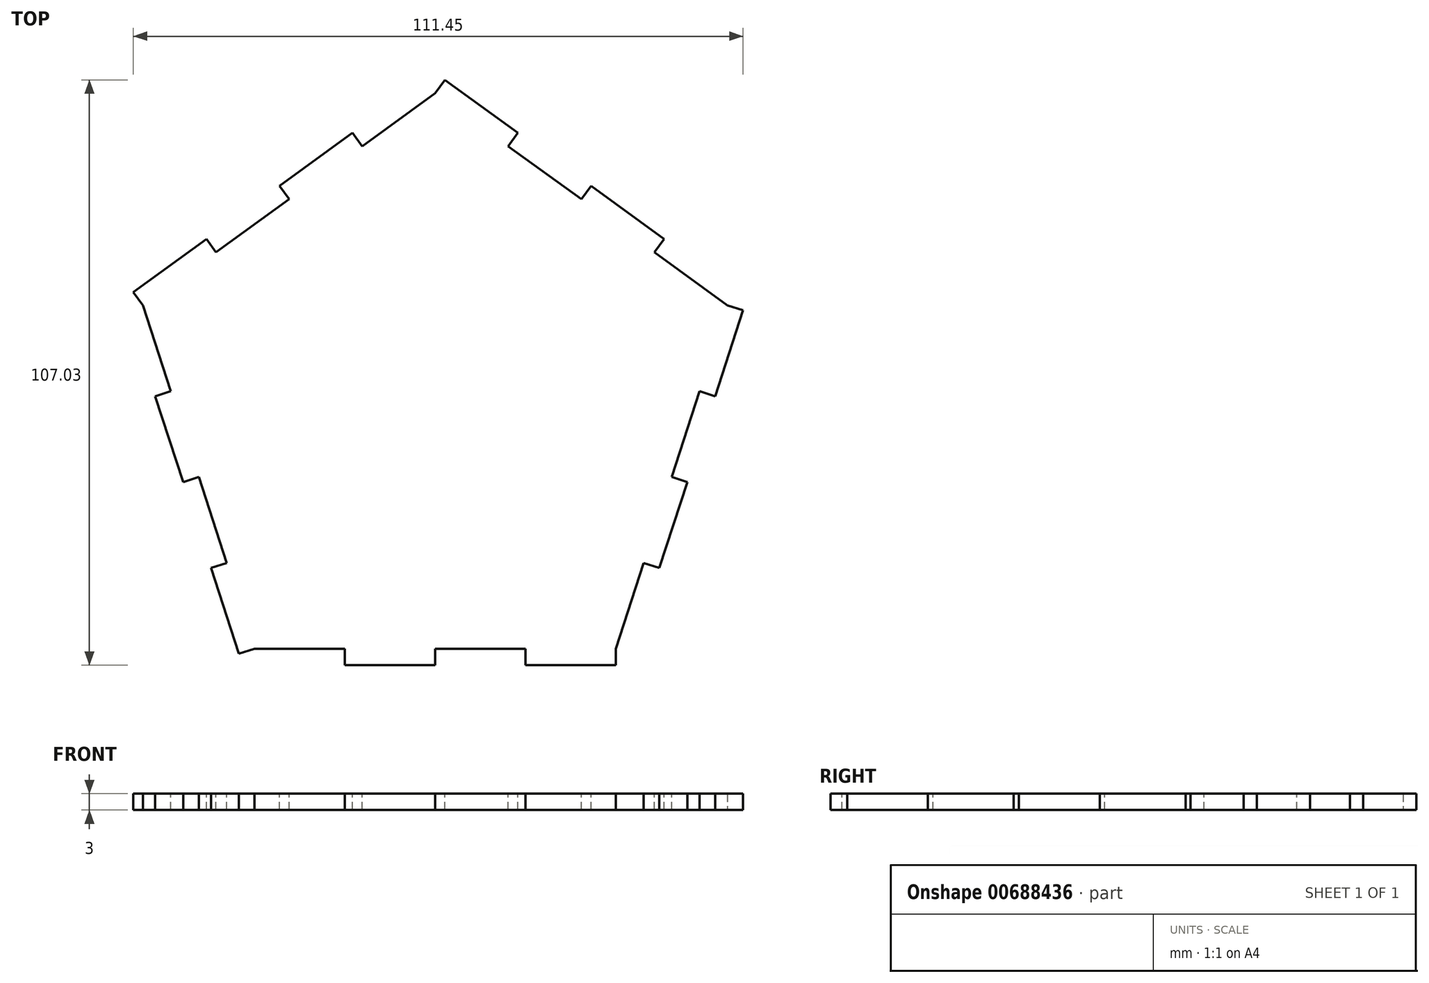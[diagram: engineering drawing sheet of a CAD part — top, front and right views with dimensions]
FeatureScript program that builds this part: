
annotation { "Feature Type Name" : "Feature", "Feature Type Description" : "" }
export const myFeature = defineFeature(function(context is Context, id is Id, definition is map)
    precondition{}
    {
        {
            var Q0;
            Q0=qCreatedBy(makeId("Top.planeOp"),FACE);
            var sketch = newSketch(context, id + "F0", { "sketchPlane" : qUnion([Q0])});
            skCircle(sketch, "E0.cCircle", {"center": v(0, 0) * mm, "radius": 56.16 * mm, "construction": true});
            skLineSegment(sketch, "E0.0", {"start": v(0, 56.16) * mm, "end": v(53.41, 17.36) * mm});
            skLineSegment(sketch, "E0.1", {"start": v(53.41, 17.36) * mm, "end": v(33.01, -45.44) * mm});
            skLineSegment(sketch, "E0.2", {"start": v(33.01, -45.44) * mm, "end": v(-33.01, -45.44) * mm});
            skLineSegment(sketch, "E0.3", {"start": v(-33.01, -45.44) * mm, "end": v(-53.41, 17.36) * mm});
            skLineSegment(sketch, "E0.4", {"start": v(-53.41, 17.36) * mm, "end": v(0, 56.16) * mm});
            skSolve(sketch);
        }
        {
            assignVariable(context, id + "F1", {"name" : "thickness", "anyValue" : 3 * mm});
        }
        {
            var Q0;
            Q0 = qSketchRegion(id + "F0", true);
            extrude(context, id + "F2", {"entities" : qUnion([Q0]), "depth" : getVariable(context, 'thickness'), "offsetDistance" : 25.4 * mm});
        }
        {
            var Q0;
            Q0=makeQuery(id+"F2.opExtrude","CAP_FACE",FACE,{"disambiguationData":[OSD([sQuery(id+"F0.wireOp",EDGE,"E0.0"),sQuery(id+"F0.wireOp",EDGE,"E0.1"),sQuery(id+"F0.wireOp",EDGE,"E0.2"),sQuery(id+"F0.wireOp",EDGE,"E0.3"),sQuery(id+"F0.wireOp",EDGE,"E0.4")])],"isStart":false});
            var sketch = newSketch(context, id + "F3", { "sketchPlane" : qUnion([Q0])});
            skLineSegment(sketch, "E1", {"start": v(1.76, 58.6) * mm, "end": v(0, 56.16) * mm});
            skLineSegment(sketch, "E2", {"start": v(1.76, 58.6) * mm, "end": v(15.12, 48.89) * mm});
            skLineSegment(sketch, "E3", {"start": v(13.35, 46.46) * mm, "end": v(15.12, 48.89) * mm});
            skLineSegment(sketch, "E4", {"start": v(13.35, 46.46) * mm, "end": v(26.7, 36.76) * mm});
            skLineSegment(sketch, "E5", {"start": v(28.47, 39.19) * mm, "end": v(26.7, 36.76) * mm});
            skLineSegment(sketch, "E6", {"start": v(28.47, 39.19) * mm, "end": v(41.82, 29.48) * mm});
            skLineSegment(sketch, "E7", {"start": v(41.82, 29.48) * mm, "end": v(40.06, 27.06) * mm});
            skLineSegment(sketch, "E8", {"start": v(40.06, 27.06) * mm, "end": v(53.41, 17.36) * mm});
            skLineSegment(sketch, "E9", {"start": v(0, 56.16) * mm, "end": v(0, 0) * mm, "construction": true});
            skLineSegment(sketch, "E10.1.0", {"start": v(-55.18, 19.78) * mm, "end": v(-41.82, 29.48) * mm});
            skLineSegment(sketch, "E10.1.1", {"start": v(-53.41, 17.36) * mm, "end": v(0, 0) * mm, "construction": true});
            skLineSegment(sketch, "E10.1.2", {"start": v(-40.06, 27.06) * mm, "end": v(-26.7, 36.76) * mm});
            skLineSegment(sketch, "E10.1.3", {"start": v(-13.35, 46.46) * mm, "end": v(0, 56.16) * mm});
            skLineSegment(sketch, "E10.1.4", {"start": v(-28.47, 39.19) * mm, "end": v(-15.12, 48.89) * mm});
            skLineSegment(sketch, "E10.1.5", {"start": v(-55.18, 19.78) * mm, "end": v(-53.41, 17.36) * mm});
            skLineSegment(sketch, "E10.1.6", {"start": v(-40.06, 27.06) * mm, "end": v(-41.82, 29.48) * mm});
            skLineSegment(sketch, "E10.1.7", {"start": v(-28.47, 39.19) * mm, "end": v(-26.7, 36.76) * mm});
            skLineSegment(sketch, "E10.1.8", {"start": v(-15.12, 48.89) * mm, "end": v(-13.35, 46.46) * mm});
            skLineSegment(sketch, "E10.2.0", {"start": v(-35.87, -46.36) * mm, "end": v(-40.97, -30.67) * mm});
            skLineSegment(sketch, "E10.2.1", {"start": v(-33.01, -45.44) * mm, "end": v(0, 0) * mm, "construction": true});
            skLineSegment(sketch, "E10.2.2", {"start": v(-38.11, -29.74) * mm, "end": v(-43.21, -14.04) * mm});
            skLineSegment(sketch, "E10.2.3", {"start": v(-48.31, 1.66) * mm, "end": v(-53.41, 17.36) * mm});
            skLineSegment(sketch, "E10.2.4", {"start": v(-46.07, -14.97) * mm, "end": v(-51.17, 0.73) * mm});
            skLineSegment(sketch, "E10.2.5", {"start": v(-35.87, -46.36) * mm, "end": v(-33.01, -45.44) * mm});
            skLineSegment(sketch, "E10.2.6", {"start": v(-38.11, -29.74) * mm, "end": v(-40.97, -30.67) * mm});
            skLineSegment(sketch, "E10.2.7", {"start": v(-46.07, -14.97) * mm, "end": v(-43.21, -14.04) * mm});
            skLineSegment(sketch, "E10.2.8", {"start": v(-51.17, 0.73) * mm, "end": v(-48.31, 1.66) * mm});
            skLineSegment(sketch, "E10.3.0", {"start": v(33.01, -48.44) * mm, "end": v(16.5, -48.44) * mm});
            skLineSegment(sketch, "E10.3.1", {"start": v(33.01, -45.44) * mm, "end": v(0, 0) * mm, "construction": true});
            skLineSegment(sketch, "E10.3.2", {"start": v(16.5, -45.44) * mm, "end": v(0, -45.44) * mm});
            skLineSegment(sketch, "E10.3.3", {"start": v(-16.5, -45.44) * mm, "end": v(-33.01, -45.44) * mm});
            skLineSegment(sketch, "E10.3.4", {"start": v(0, -48.44) * mm, "end": v(-16.5, -48.44) * mm});
            skLineSegment(sketch, "E10.3.5", {"start": v(33.01, -48.44) * mm, "end": v(33.01, -45.44) * mm});
            skLineSegment(sketch, "E10.3.6", {"start": v(16.5, -45.44) * mm, "end": v(16.5, -48.44) * mm});
            skLineSegment(sketch, "E10.3.7", {"start": v(0, -48.44) * mm, "end": v(0, -45.44) * mm});
            skLineSegment(sketch, "E10.3.8", {"start": v(-16.5, -48.44) * mm, "end": v(-16.5, -45.44) * mm});
            skLineSegment(sketch, "E10.4.0", {"start": v(56.27, 16.43) * mm, "end": v(51.17, 0.73) * mm});
            skLineSegment(sketch, "E10.4.1", {"start": v(53.41, 17.36) * mm, "end": v(0, 0) * mm, "construction": true});
            skLineSegment(sketch, "E10.4.2", {"start": v(48.31, 1.66) * mm, "end": v(43.21, -14.04) * mm});
            skLineSegment(sketch, "E10.4.3", {"start": v(38.11, -29.74) * mm, "end": v(33.01, -45.44) * mm});
            skLineSegment(sketch, "E10.4.4", {"start": v(46.07, -14.97) * mm, "end": v(40.97, -30.67) * mm});
            skLineSegment(sketch, "E10.4.5", {"start": v(56.27, 16.43) * mm, "end": v(53.41, 17.36) * mm});
            skLineSegment(sketch, "E10.4.6", {"start": v(48.31, 1.66) * mm, "end": v(51.17, 0.73) * mm});
            skLineSegment(sketch, "E10.4.7", {"start": v(46.07, -14.97) * mm, "end": v(43.21, -14.04) * mm});
            skLineSegment(sketch, "E10.4.8", {"start": v(40.97, -30.67) * mm, "end": v(38.11, -29.74) * mm});
            skPoint(sketch, "E10.center", {"position": v(0, 0) * mm});
            skSolve(sketch);
        }
        {
            var Q0;
            Q0 = qSketchRegion(id + "F3", true);
            extrude(context, id + "F4", {"entities" : qUnion([Q0]), "operationType" : NewBodyOperationType.ADD, "oppositeDirection" : true, "depth" : getVariable(context, 'thickness'), "offsetDistance" : 25.4 * mm});
        }
    });
